# Revit family: Entrance-Doors_Steel_8ft-6-Panel-Embossment_Taylor-Entrance
name_source: partatom
category: Doors
units: mm (PartAtom-declared; Revit-internal decimal feet)

## family parameters
Always vertical = Yes
Classification Number = 23.30.10.00
Cut with Voids When Loaded = No
Host = Wall
Room Calculation Point = No
Shared = No

## types (4) — shared parameters
Analytic Construction = <None>
Bottom Distance = 8.3800"
Bottom Embossment Height = 25.5000"
CAD Details = https://www.arcat.com
Define Thermal Properties by = Schematic Type
Door Height = 94.9400"
Frame Thickness = 1.4850"
Function = Interior
Height = 94.9400"
Keynote = 08 42 00
Manufacturer = Taylor Entrance Systems
Middle Embossment Height = 27.5000"
Product Page URL = https://www.arcat.com
Specification = https://www.arcat.com
Thickness = 1.7300"
Top Distance = 5.0000"
Topmost Embossment Height = 13.0000"
URL = https://www.groupenovatech.com
Wall Closure = By host

## per-type parameters (varying)
| type | B - Distance | C - Distance | Door Family | Door Width | Width |
| 2' 6" x 8' 0" | 3.3750" | 3.3750" | <By Category> | 29.7500" | 29.7500" |
| 2' 8" x 8' 0" | 4.3750" | 4.3750" | Default Wall | 31.7500" | 31.7500" |
| 2'10" x 8' 0" | 5.3750" | 5.3750" | <By Category> | 33.7500" | 33.7500" |
| 3' 0" x 8' 0" | 6.3750" | 6.3750" | <By Category> | 35.7500" | 35.7500" |

## geometry (parser evidence)
native form markers: Sweep x3
no freeform markers — native parametric forms only
